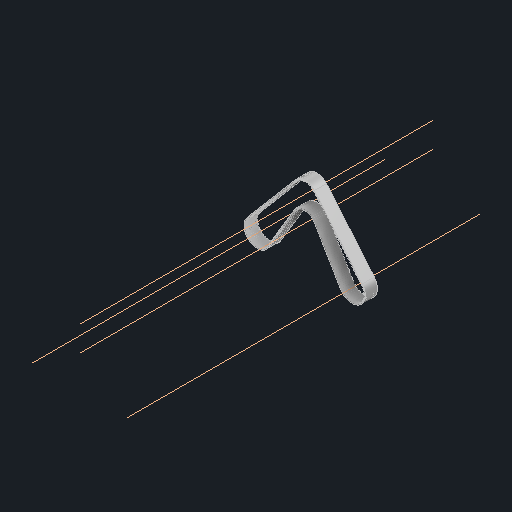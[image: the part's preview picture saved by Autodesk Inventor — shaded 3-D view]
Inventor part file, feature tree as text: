
AUTODESK INVENTOR PART (.ipt)
format: ipt  version: 2023.1 (Build 271208000, 208)  size: 1,467,904 bytes
history: native  units: mm (DEFAULTED — no unit token found)
features: other x8, plane x4, sketch x2, pattern_linear x1, sweep x1, fillet x1
ambient origin geometry x8: Origin, YZ Plane, XZ Plane, XY Plane, X Axis, Y Axis, Z Axis, Center Point
bodies: Solid1 (feature_tree)
feature tree (17):
  sketch  "Sketch Path"  dims[d2=0.0mm d4=0.3mm d5=0.3mm d6=0.0mm d7=0.0mm d8=0.0mm d9=0.0mm d10=0.0mm d11=0.0mm d12=0.0mm d14=0.2mm d15=0.2mm d20=1270.0mm d22=2.5mm d23=0.2mm d24=0.0mm d25=0.0mm]
  other  "Cross Section Plane"
  other  "Work Axis1"
  other  "Work Axis2"
  plane  "Work Plane2"
  plane  "Work Plane3"
  other  "Work Axis3"
  plane  "Work Plane4"
  other  "Work Point1"
  other  "Work Axis5"
  plane  "Work Plane5"
  other  "iSBeltToothT:1"
  pattern_linear  "Rectangular Pattern1"  Spacing1=0.3mm  [1 undecoded]
  sweep  "Belt"
  fillet  "Fillet1"  [1 undecoded]
  other  "Cross Section"
  sketch  "Sketch3"  dims[d0=10.0mm]
note: 2 required parameter values undecoded (feature->parameter linkage not recoverable at this tier; creation-order binding heuristic only, values carry confidence <= 0.55)
